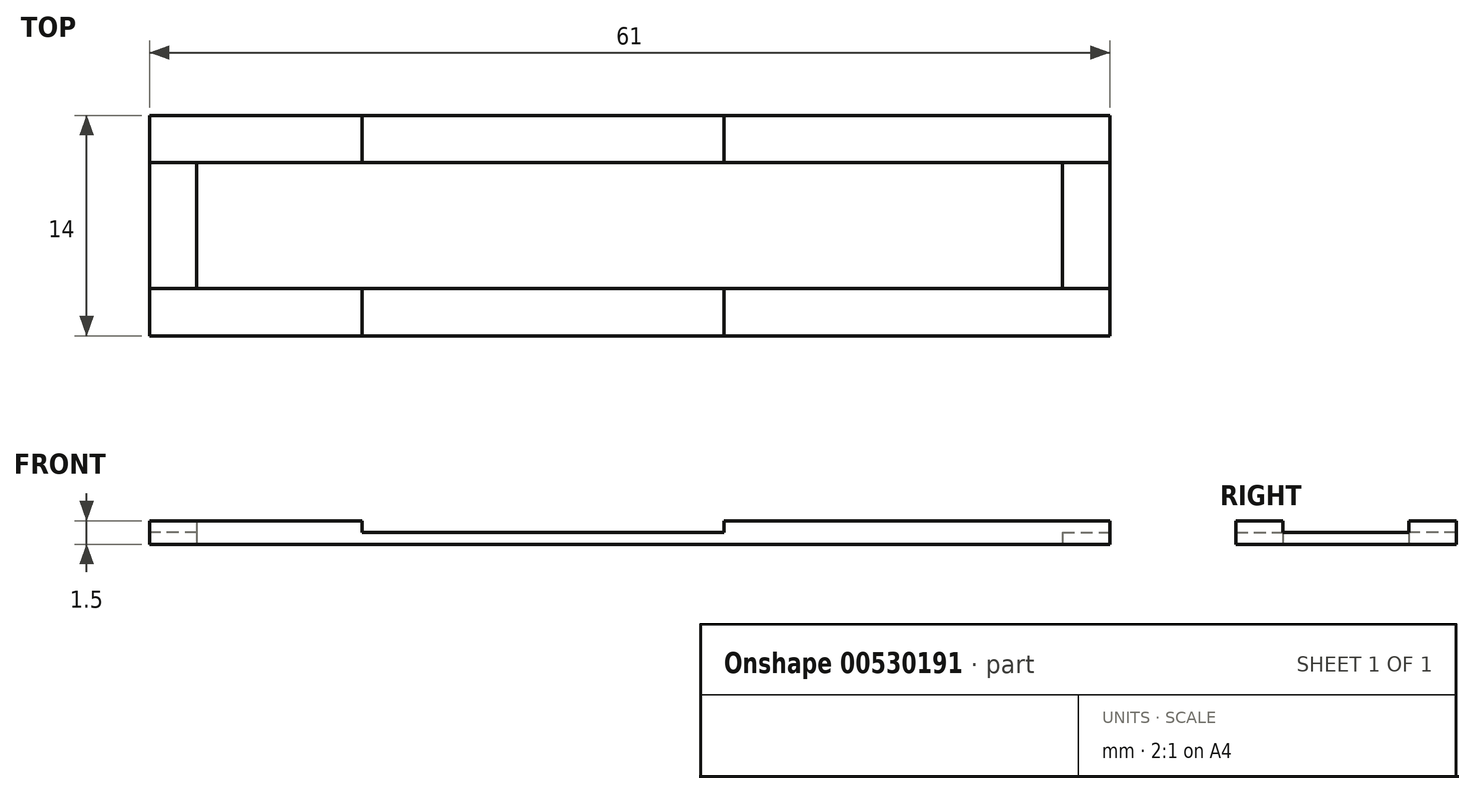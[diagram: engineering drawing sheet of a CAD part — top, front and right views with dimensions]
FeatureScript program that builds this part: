
annotation { "Feature Type Name" : "Feature", "Feature Type Description" : "" }
export const myFeature = defineFeature(function(context is Context, id is Id, definition is map)
    precondition{}
    {
        {
            var Q0;
            Q0=qCreatedBy(makeId("Top.planeOp"),FACE);
            var sketch = newSketch(context, id + "F0", { "sketchPlane" : qUnion([Q0])});
            skLineSegment(sketch, "E0.bottom", {"start": v(30.5, -7) * mm, "end": v(-30.5, -7) * mm});
            skLineSegment(sketch, "E0.top", {"start": v(30.5, 7) * mm, "end": v(-30.5, 7) * mm});
            skLineSegment(sketch, "E0.left", {"start": v(30.5, -7) * mm, "end": v(30.5, 7) * mm});
            skLineSegment(sketch, "E0.right", {"start": v(-30.5, -7) * mm, "end": v(-30.5, 7) * mm});
            skPoint(sketch, "E0.middle", {"position": v(0, 0) * mm});
            skLineSegment(sketch, "E1.bottom", {"start": v(27.5, -4) * mm, "end": v(-27.5, -4) * mm});
            skLineSegment(sketch, "E1.top", {"start": v(27.5, 4) * mm, "end": v(-27.5, 4) * mm});
            skLineSegment(sketch, "E1.left", {"start": v(27.5, -4) * mm, "end": v(27.5, 4) * mm});
            skLineSegment(sketch, "E1.right", {"start": v(-27.5, -4) * mm, "end": v(-27.5, 4) * mm});
            skLineSegment(sketch, "E2", {"start": v(-30.5, 0) * mm, "end": v(-17, 0) * mm, "construction": true});
            skPoint(sketch, "E2.endSnap0", {"position": v(-27.5, 0) * mm});
            skLineSegment(sketch, "E3", {"start": v(30.5, 0) * mm, "end": v(6, 0) * mm, "construction": true});
            skPoint(sketch, "E3.endSnap0", {"position": v(27.5, 0) * mm});
            skLineSegment(sketch, "E4", {"start": v(-17, 4) * mm, "end": v(-17, 7) * mm});
            skLineSegment(sketch, "E5", {"start": v(-17, -4) * mm, "end": v(-17, -7) * mm});
            skLineSegment(sketch, "E6", {"start": v(6, 4) * mm, "end": v(6, 7) * mm});
            skLineSegment(sketch, "E7", {"start": v(6, -4) * mm, "end": v(6, -7) * mm});
            skLineSegment(sketch, "E8.bottom", {"start": v(-30.5, 4.01) * mm, "end": v(-27.5, 4.01) * mm});
            skLineSegment(sketch, "E8.top", {"start": v(-30.5, -4) * mm, "end": v(-27.5, -4) * mm});
            skLineSegment(sketch, "E8.left", {"start": v(-30.5, 4.01) * mm, "end": v(-30.5, -4) * mm});
            skLineSegment(sketch, "E8.right", {"start": v(-27.5, 4.01) * mm, "end": v(-27.5, -4) * mm});
            skLineSegment(sketch, "E9.bottom", {"start": v(27.5, 4) * mm, "end": v(30.5, 4) * mm});
            skLineSegment(sketch, "E9.top", {"start": v(27.5, -4) * mm, "end": v(30.5, -4) * mm});
            skLineSegment(sketch, "E9.left", {"start": v(27.5, 4) * mm, "end": v(27.5, -4) * mm});
            skLineSegment(sketch, "E9.right", {"start": v(30.5, 4) * mm, "end": v(30.5, -4) * mm});
            skSolve(sketch);
        }
        {
            var Q0;
            {var subQ0=sQuery(id+"F0.wireOp",EDGE,"E0.left");Q0=makeQuery(id+"F0.imprint","IMPRINT",FACE,{"disambiguationData":[TD([[makeQuery(id+"F0.imprint","IMPRINT",EDGE,{"derivedFrom":subQ0}),1.0]])]});}
            var Q1;
            {var subQ0=sQuery(id+"F0.wireOp",EDGE,"E4");Q1=makeQuery(id+"F0.imprint","IMPRINT",FACE,{"disambiguationData":[TD([[makeQuery(id+"F0.imprint","IMPRINT",EDGE,{"derivedFrom":subQ0}),-1.0]])]});}
            var Q2;
            {var subQ3=sQuery(id+"F0.wireOp",EDGE,"E0.right");Q2=makeQuery(id+"F0.imprint","IMPRINT",FACE,{"disambiguationData":[TD([[makeQuery(id+"F0.imprint","IMPRINT",EDGE,{"derivedFrom":subQ3}),-1.0]])]});}
            var Q3;
            {var subQ0=sQuery(id+"F0.wireOp",EDGE,"E5");Q3=makeQuery(id+"F0.imprint","IMPRINT",FACE,{"disambiguationData":[TD([[makeQuery(id+"F0.imprint","IMPRINT",EDGE,{"derivedFrom":subQ0}),1.0]])]});}
            var Q4;
            {var subQ0=sQuery(id+"F0.wireOp",EDGE,"E4");Q4=makeQuery(id+"F0.imprint","IMPRINT",FACE,{"disambiguationData":[TD([[makeQuery(id+"F0.imprint","IMPRINT",EDGE,{"derivedFrom":subQ0}),1.0]])]});}
            var Q5;
            {var subQ2=sQuery(id+"F0.wireOp",EDGE,"E8.bottom");Q5=makeQuery(id+"F0.imprint","IMPRINT",FACE,{"disambiguationData":[TD([[makeQuery(id+"F0.imprint","IMPRINT",EDGE,{"derivedFrom":subQ2}),-1.0]])]});}
            var Q6;
            Q6=makeQuery(id+"F0.imprint","IMPRINT",FACE,{"disambiguationData":[TD([[makeQuery(id+"F0.imprint","IMPRINT",EDGE,{"derivedFrom":sQuery(id+"F0.wireOp",EDGE,"E9.bottom")}),-1.0]])]});
            extrude(context, id + "F1", {"entities" : qUnion([Q0, Q1, Q2, Q3, Q4, Q5, Q6]), "depth" : .75 * mm, "offsetDistance" : 25 * mm});
        }
        {
            var Q0;
            {var subQ0=sQuery(id+"F0.wireOp",EDGE,"E4");Q0=makeQuery(id+"F0.imprint","IMPRINT",FACE,{"disambiguationData":[TD([[makeQuery(id+"F0.imprint","IMPRINT",EDGE,{"derivedFrom":subQ0}),1.0]])]});}
            var Q1;
            {var subQ4=sQuery(id+"F0.wireOp",EDGE,"E5");Q1=makeQuery(id+"F0.imprint","IMPRINT",FACE,{"disambiguationData":[TD([[makeQuery(id+"F0.imprint","IMPRINT",EDGE,{"derivedFrom":subQ4}),-1.0]])]});}
            var Q2;
            {var subQ0=sQuery(id+"F0.wireOp",EDGE,"E7");Q2=makeQuery(id+"F0.imprint","IMPRINT",FACE,{"disambiguationData":[TD([[makeQuery(id+"F0.imprint","IMPRINT",EDGE,{"derivedFrom":subQ0}),1.0]])]});}
            var Q3;
            {var subQ4=sQuery(id+"F0.wireOp",EDGE,"E6");Q3=makeQuery(id+"F0.imprint","IMPRINT",FACE,{"disambiguationData":[TD([[makeQuery(id+"F0.imprint","IMPRINT",EDGE,{"derivedFrom":subQ4}),-1.0]])]});}
            extrude(context, id + "F2", {"entities" : qUnion([Q0, Q1, Q2, Q3]), "operationType" : NewBodyOperationType.ADD, "depth" : 1.5 * mm, "offsetDistance" : 25 * mm});
        }
    });
